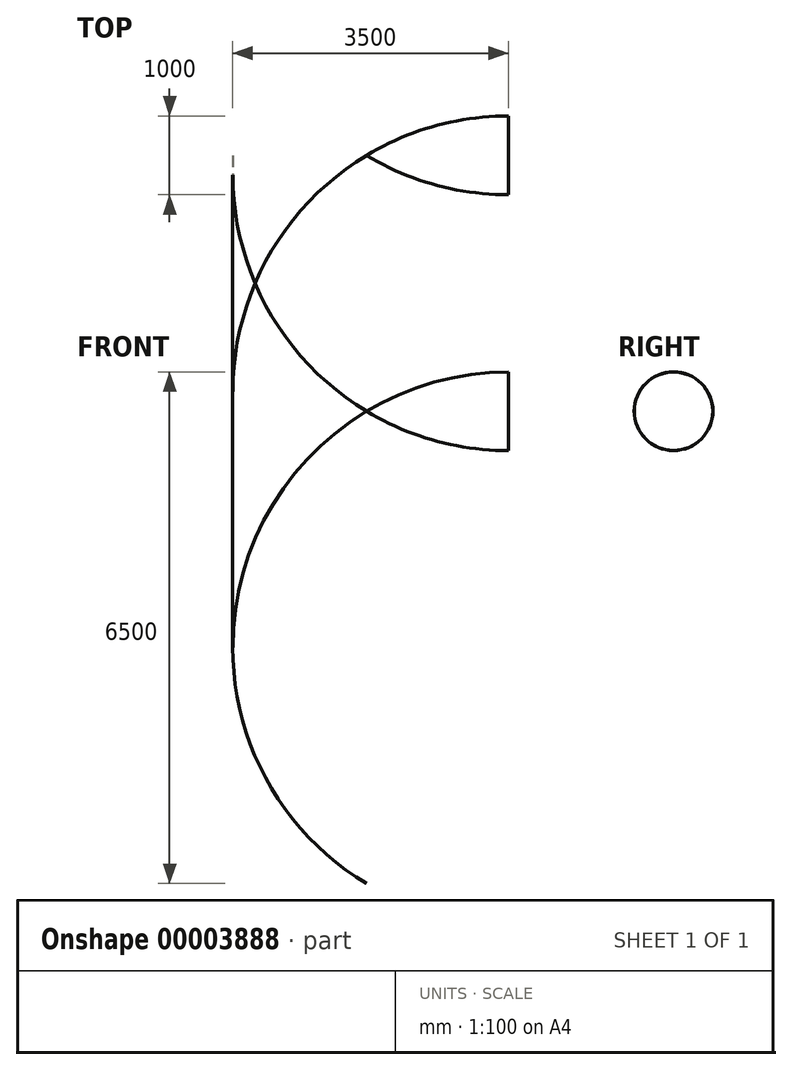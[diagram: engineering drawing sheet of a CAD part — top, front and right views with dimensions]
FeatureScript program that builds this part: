
annotation { "Feature Type Name" : "Feature", "Feature Type Description" : "" }
export const myFeature = defineFeature(function(context is Context, id is Id, definition is map)
    precondition{}
    {
        {
            var Q0;
            Q0=qCreatedBy(makeId("Front.planeOp"),FACE);
            var sketch = newSketch(context, id + "F0", { "sketchPlane" : qUnion([Q0])});
            skLineSegment(sketch, "E0", {"start": v(0, 0) * mm, "end": v(-2000, 0) * mm});
            skLineSegment(sketch, "E1", {"start": v(0, 0) * mm, "end": v(0, -1017.74) * mm});
            skCircle(sketch, "E2", {"center": v(0, -3000) * mm, "radius": 3500 * mm});
            skLineSegment(sketch, "E3", {"start": v(0, 0) * mm, "end": v(0, 749.36) * mm});
            skSolve(sketch);
        }
        {
            var Q0;
            {var subQ0=sQuery(id+"F0.wireOp",EDGE,"E3");var subQ3=sQuery(id+"F0.wireOp",EDGE,"E0");var subQ4=makeQuery(id+"F0.imprint","INTERSECT",VERTEX,{"derivedFrom":[subQ3,subQ0]});Q0=makeQuery(id+"F0.imprint","IMPRINT",FACE,{"disambiguationData":[TD([[makeQuery(id+"F0.imprint","IMPRINT",EDGE,{"disambiguationData":[TD([[subQ4,-1.0]])],"derivedFrom":subQ3}),-1.0]])]});}
            var Q1;
            Q1=sQuery(id+"F0.wireOp",EDGE,"E0");
            revolve(context, id + "F1", {"entities" : qUnion([Q0]), "axis" : qUnion([Q1]), "revolveType" : RevolveType.FULL});
        }
        {
            var Q0;
            Q0=makeQuery(id+"F1.opRevolve","SWEPT_FACE",FACE,{"disambiguationData":[OSD([sQuery(id+"F0.wireOp",EDGE,"E3")])]});
            shell(context, id + "F2", {"entities" : qUnion([Q0]), "thickness" : 2.5 * mm});
        }
    });
